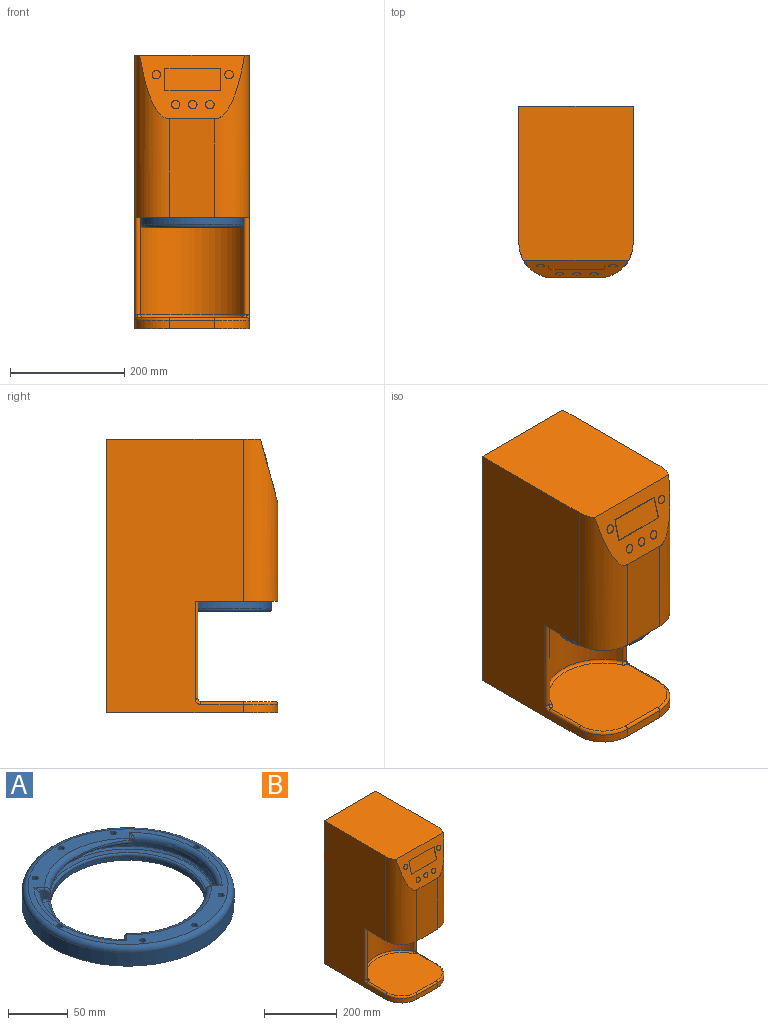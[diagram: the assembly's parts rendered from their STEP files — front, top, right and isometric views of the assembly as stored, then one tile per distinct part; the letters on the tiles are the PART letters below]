
ASSEMBLY  parts=2 mates=1
PART A: 96 faces, bbox 194x194x20.1 mm
  f0: bspline ~37.41x35.38mm, area 14.4mm2, adj f28,f51,f82,f93
  f1: bspline ~37.41x35.38mm, area 11.9mm2, adj f6,f27,f55,f88
  f2: cylinder r=65mm len=130mm, axis (0,0,-1), area 1941.2mm2, adj f6,f27,f28,f33,f34,f38,f41,f51
  f3: plane 0.47x0.02mm, normal (0.68,-0.74,0), area 0mm2, adj f7,f15,f54,f58
  f4: bspline ~118.94x45.39mm, area 42.9mm2, adj f7,f11,f15,f27,f54,f58,f63
  f5: bspline ~118.94x45.39mm, area 431.6mm2, adj f6,f46,f48,f56,f88
  f6: bspline ~39.94x21.92mm, area 104.3mm2, adj f1,f2,f5,f27,f48,f55,f56
  f7: bspline ~3.58x3.53mm, area 0.1mm2, adj f3,f4,f15,f54
  f8: plane 4.2x1.49mm, normal (-0.68,0.74,0), area 0.1mm2, adj f12,f16,f29,f53,f59,f60
  f9: plane 2.72x2.5mm, normal (-0.68,0.74,0), area 0.6mm2, adj f42,f43,f81,f90
  f10: plane 2.72x2.5mm, normal (0.68,-0.74,0), area 0.6mm2, adj f44,f45,f46,f85
  f11: plane 119.25x119.13mm, normal (0,0,1), area 1022.9mm2, adj f4,f58,f62,f66,f95
  f12: plane 119.22x118.82mm, normal (0,0,1), area 1018mm2, adj f8,f52,f59,f60,f61,f72,f94
  f13: plane 8.3x4.18mm, normal (-0.68,-0.74,0), area 40.2mm2, adj f39,f40,f41,f72,f74,f75
  f14: plane 8.3x4.18mm, normal (0.68,0.74,0), area 40.2mm2, adj f36,f37,f38,f66,f68,f69
  f15: cylinder r=74mm len=124.43mm, axis (0,0,-1), area 806.6mm2, adj f3,f4,f7,f27,f35,f58,f68,f87
  f16: cylinder r=74mm len=124.43mm, axis (0,0,-1), area 806.3mm2, adj f8,f28,f29,f32,f60,f74,f92,f93
  f17: cylinder r=2.5mm len=18.8mm, axis (0,0,-1), area 295.3mm2, adj f26,f83
  f18: cylinder r=2.5mm len=18.8mm, axis (0,0,-1), area 295.3mm2, adj f26,f83
  f19: cylinder r=2.5mm len=18.8mm, axis (0,0,-1), area 295.3mm2, adj f26,f83
  f20: cylinder r=2.5mm len=18.8mm, axis (0,0,-1), area 295.3mm2, adj f26,f35,f83
  f21: cylinder r=2.5mm len=18.8mm, axis (0,0,-1), area 295.3mm2, adj f26,f32,f83
  f22: cylinder r=2.5mm len=18.8mm, axis (0,0,-1), area 295.3mm2, adj f26,f83
  f23: cylinder r=2.5mm len=18.8mm, axis (0,0,-1), area 295.3mm2, adj f26,f83
  f24: cylinder r=2.5mm len=18.8mm, axis (0,0,-1), area 295.3mm2, adj f26,f83
  f25: cylinder r=89mm len=178mm, axis (0,0,-1), area 7717mm2, adj f31,f83
  f26: plane 168x168mm, normal (0,0,1), area 4550.6mm2, adj f17,f18,f19,f20,f21,f22,f23,f24
  f27: plane 8.08x6.66mm, normal (0.73,0.68,0), area 36.9mm2, adj f1,f2,f4,f6,f15,f63,f88
  f28: plane 8.08x6.66mm, normal (-0.73,-0.68,0), area 36.9mm2, adj f0,f2,f16,f29,f64,f82,f93
  f29: bspline ~118.94x45.39mm, area 46.3mm2, adj f8,f16,f28,f52,f53,f59,f64
  f30: bspline ~118.94x45.39mm, area 431.6mm2, adj f49,f78,f79,f81,f93
  f31: torus R=84mm, axis (0,0,1), area 4302.3mm2, adj f25,f26
  f32: torus R=79mm, axis (0,0,1), area 871.1mm2, adj f16,f21,f26,f75,f76,f89,f90,f91
  f33: torus R=70mm, axis (0,0,1), area 629.7mm2, adj f2,f26,f40,f45,f48
  f34: torus R=70mm, axis (0,0,1), area 629.7mm2, adj f2,f26,f37,f43,f79
  f35: torus R=79mm, axis (0,0,1), area 871.1mm2, adj f15,f20,f26,f69,f70,f84,f85,f86
  f36: cylinder r=2mm len=7.98mm, axis (0.74,-0.68,0), area 18.3mm2, adj f14,f26,f37,f70
  f37: bspline ~6.12x5.82mm, area 20.8mm2, adj f14,f34,f36,f38
  f38: cylinder r=2mm len=9.3mm, axis (0,0,-1), area 22.5mm2, adj f2,f14,f37,f65
  f39: cylinder r=2mm len=7.98mm, axis (-0.74,0.68,0), area 18.3mm2, adj f13,f26,f40,f76
  f40: bspline ~6.12x5.82mm, area 20.8mm2, adj f13,f33,f39,f41
  f41: cylinder r=2mm len=9.3mm, axis (0,0,-1), area 22.5mm2, adj f2,f13,f40,f71
  f42: cylinder r=2mm len=7.98mm, axis (0.74,0.68,0), area 18.3mm2, adj f9,f26,f43,f89
  f43: bspline ~3.81x3.75mm, area 4.6mm2, adj f9,f34,f42,f80
  f44: cylinder r=2mm len=7.98mm, axis (-0.74,-0.68,0), area 18.3mm2, adj f10,f26,f45,f84
  f45: bspline ~3.81x3.75mm, area 4.6mm2, adj f10,f33,f44,f47
  f46: bspline ~6.32x6.03mm, area 9.7mm2, adj f5,f10,f47,f86,f87
  f47: sphere r=2mm, area 10.3mm2, adj f45,f46,f48
  f48: bspline ~72.72x28.03mm, area 287.8mm2, adj f5,f6,f33,f47
  f49: plane 46.93x24.34mm, normal (0,0,-1), area 54.7mm2, adj f30,f50,f51,f77,f93
  f50: cylinder r=73.97mm len=45.63mm, axis (0,0,-1), area 45.9mm2, adj f49,f51,f93
  f51: plane 6.89x5.92mm, normal (-0.76,-0.65,0), area 2.5mm2, adj f0,f2,f49,f50,f77,f82,f93
  f52: plane 5.55x4.76mm, normal (-0.76,-0.65,0), area 0.1mm2, adj f12,f29,f59,f61,f64
  f53: cylinder r=73.97mm len=53.08mm, axis (0,0,-1), area 65.8mm2, adj f8,f29,f59
  f54: cylinder r=73.97mm len=62.3mm, axis (0,0,-1), area 87mm2, adj f3,f4,f7,f58
  f55: plane 6.01x5.23mm, normal (0.75,0.66,0), area 2.4mm2, adj f1,f6,f56,f57,f88
  f56: plane 47.33x25.32mm, normal (0,0,-1), area 61.2mm2, adj f5,f6,f55,f57,f88
  f57: cylinder r=73.97mm len=46.03mm, axis (0,0,-1), area 46.9mm2, adj f55,f56,f88
  f58: torus R=72mm, axis (0,0,1), area 606.4mm2, adj f3,f4,f11,f15,f54,f67
  f59: torus R=71.97mm, axis (0,0,1), area 292.8mm2, adj f8,f12,f29,f52,f53
  f60: torus R=72mm, axis (0,0,1), area 335.9mm2, adj f8,f12,f16,f73
  f61: torus R=67mm, axis (0,0,1), area 621.8mm2, adj f2,f12,f52,f71,f94
  f62: torus R=67mm, axis (0,0,1), area 623mm2, adj f2,f11,f63,f65,f95
  f63: bspline ~11.23x10.39mm, area 7.5mm2, adj f2,f4,f27,f62
  f64: bspline ~11.33x10.45mm, area 8.6mm2, adj f2,f28,f29,f52
  f65: bspline ~4.35x4mm, area 4.5mm2, adj f38,f62,f66
  f66: cylinder r=2mm len=5.04mm, axis (-0.74,0.68,0), area 15.7mm2, adj f11,f14,f65,f67
  f67: sphere r=2mm, area 6.4mm2, adj f58,f66,f68
  f68: cylinder r=2mm len=5.3mm, axis (0,0,-1), area 16.9mm2, adj f14,f15,f67,f69
  f69: bspline ~5.9x3.64mm, area 8.1mm2, adj f14,f35,f68,f70
  f70: bspline ~6.14x3.55mm, area 6.8mm2, adj f35,f36,f69
  f71: bspline ~4.35x4mm, area 4.5mm2, adj f41,f61,f72
  f72: cylinder r=2mm len=5.04mm, axis (0.74,-0.68,0), area 15.7mm2, adj f12,f13,f71,f73
  f73: sphere r=2mm, area 6.4mm2, adj f60,f72,f74
  f74: cylinder r=2mm len=5.3mm, axis (0,0,-1), area 16.9mm2, adj f13,f16,f73,f75
  f75: bspline ~5.9x3.64mm, area 8.1mm2, adj f13,f32,f74,f76
  f76: bspline ~6.14x3.55mm, area 6.8mm2, adj f32,f39,f75
  f77: torus R=67mm, axis (0,0,1), area 13.8mm2, adj f2,f49,f51,f78
  f78: bspline ~34.04x16.5mm, area 84.1mm2, adj f2,f30,f77,f79
  f79: bspline ~72.72x28.03mm, area 287.8mm2, adj f30,f34,f78,f80
  f80: sphere r=2mm, area 8.7mm2, adj f43,f79,f81
  f81: bspline ~6.32x6.03mm, area 9.7mm2, adj f9,f30,f80,f91,f92
  f82: bspline ~11.66x10.9mm, area 8.6mm2, adj f0,f2,f28,f51
  f83: plane 178x178mm, normal (0,0,-1), area 11415mm2, adj f2,f17,f18,f19,f20,f21,f22,f23
  f84: bspline ~6.14x3.55mm, area 6.8mm2, adj f35,f44,f85
  f85: bspline ~2.97x1.73mm, area 0.5mm2, adj f10,f35,f84,f86
  f86: bspline ~3.87x3.54mm, area 5.7mm2, adj f35,f46,f85,f87
  f87: bspline ~3.84x2.96mm, area 6.6mm2, adj f15,f46,f86,f88
  f88: bspline ~109.25x27.21mm, area 278.9mm2, adj f1,f5,f15,f27,f55,f56,f57,f87
  f89: bspline ~6.14x3.55mm, area 6.8mm2, adj f32,f42,f90
  f90: bspline ~2.97x1.73mm, area 0.5mm2, adj f9,f32,f89,f91
  f91: bspline ~3.87x3.54mm, area 5.7mm2, adj f32,f81,f90,f92
  f92: bspline ~3.84x2.96mm, area 6.6mm2, adj f16,f81,f91,f93
  f93: bspline ~109.25x27.21mm, area 280.3mm2, adj f0,f16,f28,f30,f49,f50,f51,f92
  f94: cylinder r=2.5mm len=6.5mm, axis (0,0,-1), area 102.1mm2, adj f12,f61,f83
  f95: cylinder r=2.5mm len=6.5mm, axis (0,0,-1), area 102.1mm2, adj f11,f62,f83
PART B: 47 faces, bbox 219.3x305x480 mm
  f0: plane 270x200mm, normal (0,0,1), area 53843.8mm2, adj f2,f3,f5,f6,f7,f15,f18
  f1: plane 172.12x80mm, normal (0,-1,0), area 13763.1mm2, adj f2,f3,f14,f18
  f2: cylinder r=60mm len=284mm, axis (0,0,-1), area 22165.2mm2, adj f0,f1,f6,f14,f18
  f3: cylinder r=60mm len=284mm, axis (0,0,-1), area 22166.3mm2, adj f0,f1,f14,f15,f18
  f4: cylinder r=100mm len=180.95mm, axis (0,0,-1), area 38674.1mm2, adj f14,f16,f17,f35
  f5: plane 480x200mm, normal (0,1,0), area 96000mm2, adj f0,f6,f7,f8
  f6: plane 480x239.98mm, normal (-1,0,0), area 99881mm2, adj f0,f2,f5,f8,f11,f14,f17,f37
  f7: plane 480.01x200.01mm, normal (1,0,0), area 87927.4mm2, adj f0,f5,f8,f10,f14,f15,f16,f41
  f8: plane 300.02x200mm, normal (0,0,-1), area 58454.9mm2, adj f5,f6,f7,f9,f10,f11,f12
  f9: cylinder r=60mm len=60.03mm, axis (0,0,-1), area 1415.2mm2, adj f8,f10,f12,f42
  f10: plane 40.02x15.01mm, normal (1,0,0), area 600.7mm2, adj f7,f8,f9,f44
  f11: cylinder r=60mm len=60mm, axis (0,0,-1), area 1414.1mm2, adj f6,f8,f12,f39
  f12: plane 80x15.01mm, normal (0,-1,0), area 1200.8mm2, adj f8,f9,f11,f40
  f13: plane 190.03x190.02mm, normal (0,0,1), area 31096.8mm2, adj f34,f35,f36,f38,f39,f40,f42,f43
  f14: plane 200.02x200mm, normal (0,0,-1), area 34136.8mm2, adj f1,f2,f3,f4,f6,f7,f15,f16
  f15: plane 284x40.02mm, normal (1,0,0), area 11366.5mm2, adj f0,f3,f7,f14
  f16: cylinder r=5mm len=171mm, axis (0,0,-1), area 2309.9mm2, adj f4,f7,f14,f36
  f17: cylinder r=5mm len=171mm, axis (0,0,-1), area 2309.9mm2, adj f4,f6,f14,f34
  f18: plane 183.92x112.05mm, normal (0,-0.97,0.26), area 13040.2mm2, adj f0,f1,f2,f3,f19,f20,f21,f22
  f19: plane 97.3x0.97mm, normal (0,0.26,0.97), area 97.3mm2, adj f18,f20,f22,f23
  f20: plane 38.9x11.32mm, normal (-1,0,0), area 40mm2, adj f18,f19,f21,f23
  f21: plane 97.3x0.97mm, normal (0,-0.26,-0.97), area 97.3mm2, adj f18,f20,f22,f23
  f22: plane 38.9x11.32mm, normal (1,0,0), area 40mm2, adj f18,f19,f21,f23
  f23: plane 97.3x38.64mm, normal (0,-0.97,0.26), area 3892mm2, adj f19,f20,f21,f22
  f24: cylinder r=7.5mm len=15mm, axis (0,0.97,-0.26), area 23.6mm2, adj f18,f25
  f25: plane 15x14.49mm, normal (0,-0.97,0.26), area 176.7mm2, adj f24
  f26: cylinder r=7.5mm len=15mm, axis (0,0.97,-0.26), area 23.6mm2, adj f18,f27
  f27: plane 15x14.49mm, normal (0,-0.97,0.26), area 176.7mm2, adj f26
  f28: cylinder r=7.5mm len=15mm, axis (0,0.97,-0.26), area 23.6mm2, adj f18,f29
  f29: plane 15x14.49mm, normal (0,-0.97,0.26), area 176.7mm2, adj f28
  f30: cylinder r=7.5mm len=15mm, axis (0,0.97,-0.26), area 23.6mm2, adj f18,f31
  f31: plane 15x14.49mm, normal (0,-0.97,0.26), area 176.7mm2, adj f30
  f32: cylinder r=7.5mm len=15mm, axis (0,0.97,-0.26), area 23.6mm2, adj f18,f33
  f33: plane 15x14.49mm, normal (0,-0.97,0.26), area 176.7mm2, adj f32
  f34: torus R=10mm, axis (0,0,1), area 62.5mm2, adj f13,f17,f35,f37
  f35: torus R=95mm, axis (0,0,1), area 1744mm2, adj f4,f13,f34,f36
  f36: torus R=10mm, axis (0,0,1), area 62.5mm2, adj f13,f16,f35,f41
  f37: bspline ~11.12x9.99mm, area 82mm2, adj f6,f34,f38
  f38: cylinder r=4.99mm len=74.7mm, axis (0,1,0), area 585.5mm2, adj f6,f13,f37,f39
  f39: torus R=55.01mm, axis (0,0,1), area 716.2mm2, adj f11,f13,f38,f40
  f40: cylinder r=4.99mm len=80mm, axis (-1,0,0), area 627.1mm2, adj f12,f13,f39,f42
  f41: bspline ~12.23x9.99mm, area 82mm2, adj f7,f36,f43
  f42: torus R=55.01mm, axis (0,0,1), area 716.7mm2, adj f9,f13,f40,f44
  f43: cylinder r=4.99mm len=34.72mm, axis (0,-1,0), area 272.2mm2, adj f7,f13,f41,f44
  f44: cylinder r=4.99mm len=40.02mm, axis (0,-1,0), area 313.7mm2, adj f10,f13,f42,f43
  f45: cylinder r=9mm len=18mm, axis (0,0,-1), area 226.2mm2, adj f14,f46
  f46: plane 18x18mm, normal (0,0,-1), area 254.5mm2, adj f45
PLACE A rot(axis=(0,1,0),180deg) t=(-250.61,-61.6,170.72)mm
PLACE B t=(-250.61,-61.6,-26.48)mm
MATE cylindrical A.f25 <-> B.f45  axis (0,0,1) through (-250.61,-61.6,169.52)mm
